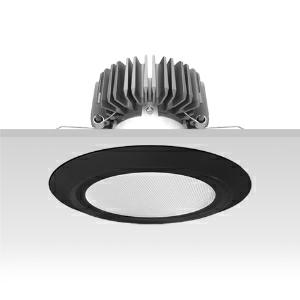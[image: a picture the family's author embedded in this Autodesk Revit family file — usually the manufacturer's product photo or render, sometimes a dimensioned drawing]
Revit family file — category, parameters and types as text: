
# Revit family: 3f_filippi_-_3f_reno_bianco_ampio_3f_filippi_-_30637_a01038_-_3f_reno_200_wh_4000-840_wide___vs_bk_3cdb
name_source: partatom
category: Lighting Fixtures
units: mm (PartAtom-declared; Revit-internal decimal feet)

## family parameters
Cut with Voids When Loaded = No
Host = Face
Light Source = No
Part Type = Normal
Room Calculation Point = No
Round Connector Dimension = Use Diameter
Shared = No

## types (1)
- 3F Filippi - 3F Reno Bianco Ampio (1 x LED, 3089 lm, 36 W, 4000 K)
    Apparent Load = 36 VA
    Approval mark = CE
    CIE Flux Codes = 75 94 99 100 100
    Color Rendering = 80
    Color Temperature = 4000 K
    Control Gear = Electronic ballast
    Default Elevation = 1800 mm
    Description = ILLUMINOTECHNICAL
Luminous efficiency 100% (DLOR 100%, ULOR 0%).
Initial luminous flux of the luminaire 3089 lm.
Direct symmetric wide distribution.
Installation Interdistance Transv.D = 1.16 x hu - Long.D = 1.14 x hu.
Tabular UGR (CIE 117 - 4H-8H; S=0.25H; 70/50/20): RUG 22.5 - 22.4.
Beam angle: 74° - 74°.
Luminous efficacy 86 lm/W.
Lifetime (L90/B10): 30000 h. (tq+25°C)
Lifetime (L85/B10): 50000 h. (tq+25°C)
Lifetime (L70/B10): 80000 h. (tq+25°C)
Sudden decreased luminous flux after 50000 hours: 0% (C0).
Photobiological safety in compliance with IEC/TR 62778: RG1 low risk, (IEC 62471).
In compliance with IEC/EN 62722-2-1 - IEC/EN 62717 standards.

SOURCE
Compact LED module 4000/840.
Energy efficiency class (UE 2019/2020 - UE 2019/2015): E.
CIE 13.3 Colour rendering index: CRI >80 (R9 <50%).
IES TM-30 Fidelity Index: Rf = 84 Rg = 95.
CCT nominal colour temperature 4000 K.
Colour initial tolerance (MacAdam): SDCM 3.
Zhaga Book 3 compliant.

MECHANICAL
Passive heat dissipator in die-casting aluminium, oversized, for optimum thermal management of the LED module.
Parabolic element with graduated/concentric rings in white polycarbonate.
Transparent external lens with glossy and satin differentiated surfaces, with a cooling and anti-insect system in methacrylate (PMMA).
Fastening spring clips in stainless steel.
Dimensions: diameter 226 mm, height 146 mm. Weight 1.785 kg.
IP44 protection degree for exposed part, IP20 for recessed part.
Mechanical strength to impacts IK06 (1 joule).
Glow-wire test resistance 650°C.

ELECTRICAL
Wiring on a separate unit.
Halogen Free electronic wiring 230V-50/60Hz, power factor 0.95, THD <25%, constant output current, SELV, class II, 1 driver.
Power of the luminaire 36 W.
ENEC - CE.
SAFE FLICKER: PstLM=<1 and SVM=<0.4 (IEC TR 61547-1 and IEC TR 63158), to ensure a more comfortable and safe light.
Luminaire compliant with EN 60598-2-22 for power supply from a centralised emergency system CPSS (Central Power Supply System), not incorporated in the luminaire - high risk areas excluded. The default power and flux are 100% in AC and 100% in DC.
Ambient temperature from 0°C to +25°C.
Temperature class T6 max 85°C.
Relative humidity UR: <85%.

INSTALLATION
Pull-up recessed fitting.
False ceiling carving: 200 mm.
All accessories dedicated to this product are available on the Catalog and on our website www.3F-Filippi.com.

ACCESSORIES
A01038 - Anti-glare microprismatic VS moulded glass, tempered, not flammable, locked and in line with the trim, in black polycarbonate.

APPLICATIONS
Environments: architectural, commercial, exhibition areas, transit areas, corridors, shops, display windows, service areas.
In false ceilings with narrow voids.

WARNING
Luminaire designed for disposal/recycling at end-of-life.
Replaceable (LED only) light source by a professional. Replaceable control gear by a professional.
    Height = 0 mm  [stored 0 ft]
    Lamp = 1 x LED
    Lamp Light Flux = 3089 lm
    Lamp Power = 36 W
    Lamp count = 1
    Length = 226 mm
    Lifetime = 50000 h
    Luminous efficacy = 86 lm/W
    Manufacturer = 3F Filippi
    ModVariant = No
    Model = 3F Filippi - 30637+A01038 - 3F Reno 200 WH 4000-840 WIDE + VS BK
    Mounting Place = Ceiling
    Mounting Type = Recessed
    Number of Poles = 1
    OnlyDefault = Yes
    Power Factor = 1
    Product Name = 3F Filippi - 3F Reno Bianco Ampio
    Product group = recessed luminaire
    ProductGroupID = 4
    Protection Class = Protection class II
    Protection Degree = IP 20
    RLX_Detail_Level = 1
    RLX_Emergency_Light_Flux = 0 lm
    RLX_Emergency_Type = 0
    RLX_Emergency_Type_DB = No
    RlxData = <blob elided: 97065 chars, md5=77d09345>
    Socket = socket
    Standby Power = 0 W
    System Light Flux = 3089 lm
    System Power = 36 W
    Type Comments = Product without accessories
    Type Image = 3ffilippi_3f_reno_200_bk_vs_smp.jpg
    URL = http://relux.com
    VarID = ---
    Voltage = 0 V
    Weight = 0.00 kg
    Width = 0 mm  [stored 0 ft]

note: [stored X ft] marks values corroborated as IEEE doubles in the binary element streams (Revit-internal decimal feet)

## geometry (parser evidence)
native form markers: Blend x4, Sweep x10
no freeform markers — native parametric forms only
